FCSTD DOCUMENT  (FreeCAD 0.20R29177 (Git))
Label: contour
License: All rights reserved
LicenseURL: http://en.wikipedia.org/wiki/All_rights_reserved
objects: Sketcher::SketchObject×1, PartDesign::Body×1
note: 2 computed .brp shape members not serialized (recipe doc carries the construction recipe); baked Part::Feature solids carry a one-line shape summary decoded from their .brp

FEATURE [Sketcher::SketchObject] Sketch
  FullyConstrained = true
  MapMode = 5
  Support = -> [XY_Plane]
  sketch-geometry (8):
    g0: LineSegment StartX=-14.1421 StartY=5 StartZ=0 EndX=-20 EndY=5 EndZ=0
    g1: LineSegment StartX=-20 StartY=5 StartZ=0 EndX=-20 EndY=-5 EndZ=0
    g2: LineSegment StartX=-20 StartY=-5 StartZ=0 EndX=-14.1421 EndY=-5 EndZ=0
    g3: LineSegment StartX=14.1421 StartY=5 StartZ=0 EndX=20 EndY=5 EndZ=0
    g4: LineSegment StartX=20 StartY=5 StartZ=0 EndX=20 EndY=-5 EndZ=0
    g5: LineSegment StartX=20 StartY=-5 StartZ=0 EndX=14.1421 EndY=-5 EndZ=0
    g6: ArcOfCircle CenterX=0 CenterY=0 CenterZ=0 NormalX=0 NormalY=0 NormalZ=1 AngleXU=0 Radius=15 StartAngle=0.339837 EndAngle=2.80176
    g7: ArcOfCircle CenterX=0 CenterY=0 CenterZ=0 NormalX=0 NormalY=0 NormalZ=1 AngleXU=0 Radius=15 StartAngle=3.48143 EndAngle=5.94335
  constraints (24):
    c: Horizontal(g0)
    c: Coincident(g0,g1)
    c: Vertical(g1)
    c: Coincident(g1,g2)
    c: Horizontal(g2)
    c: Horizontal(g3)
    c: Coincident(g3,g4)
    c: Vertical(g4)
    c: Coincident(g4,g5)
    c: Coincident(g6,g-1)
    c: Coincident(g6,g0)
    c: Coincident(g6,g3)
    c: Coincident(g7,g6)
    c: Coincident(g7,g2)
    c: Coincident(g7,g5)
    c: Horizontal(g5)
    c: Equal(g3,g5)
    c: Equal(g4,g1)
    c: Equal(g0,g2)
    c: Equal(g7,g6)
    c: Equal(g0,g3)
    c: Distance(g0,g3) = 40
    c: Radius(g6) = 15
    c: Distance(g4) = 10
FEATURE [PartDesign::Body] Body
  Group = -> [Sketch]
  Origin = -> Origin
